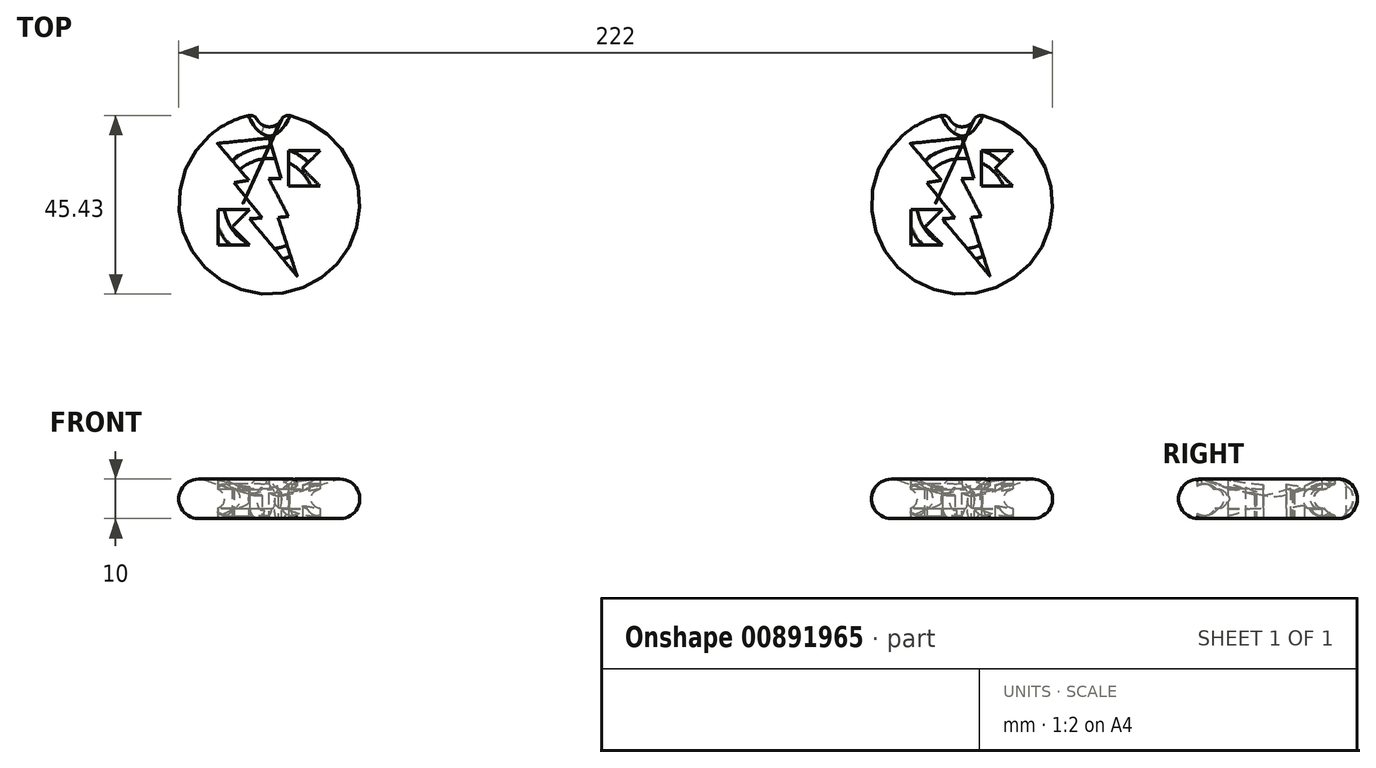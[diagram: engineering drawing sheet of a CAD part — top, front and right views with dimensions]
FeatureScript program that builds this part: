
annotation { "Feature Type Name" : "Feature", "Feature Type Description" : "" }
export const myFeature = defineFeature(function(context is Context, id is Id, definition is map)
    precondition{}
    {
        {
            var Q0;
            Q0=qCreatedBy(makeId("Right.planeOp"),FACE);
            var sketch = newSketch(context, id + "F0", { "sketchPlane" : qUnion([Q0])});
            skArc(sketch, "E0", {"start": v(-47.98, 20.03) * mm, "mid": v(-54.65, 16.24) * mm, "end": v(-49.73, 10.35) * mm});
            skArc(sketch, "E1", {"start": v(-47.98, 20.03) * mm, "mid": v(-39.95, 17.37) * mm, "end": v(-31.73, 15.35) * mm});
            skLineSegment(sketch, "E2", {"start": v(-31.73, 10.35) * mm, "end": v(-31.73, 15.35) * mm});
            skPoint(sketch, "E3.orphan", {"position": v(-49.73, 20.7) * mm});
            skLineSegment(sketch, "E4", {"start": v(-49.73, 10.35) * mm, "end": v(-31.73, 10.35) * mm});
            skSolve(sketch);
        }
        {
            var Q0;
            Q0 = qSketchRegion(id + "F0", true);
            var Q1;
            Q1=sQuery(id+"F0.wireOp",EDGE,"E2");
            revolve(context, id + "F1", {"surfaceOperationType" : NewSurfaceOperationType.NEW, "entities" : qUnion([Q0]), "axis" : qUnion([Q1]), "revolveType" : RevolveType.FULL});
        }
        {
            var Q0;
            Q0=qCreatedBy(makeId("Top.planeOp"),FACE);
            var sketch = newSketch(context, id + "F2", { "sketchPlane" : qUnion([Q0])});
            skLineSegment(sketch, "E5", {"start": v(-0.22, -15) * mm, "end": v(-0.08, -15.05) * mm});
            skLineSegment(sketch, "E6", {"start": v(-0.08, -15.05) * mm, "end": v(2.99, -25.32) * mm});
            skLineSegment(sketch, "E7", {"start": v(2.99, -25.32) * mm, "end": v(-0.17, -25.32) * mm});
            skLineSegment(sketch, "E8", {"start": v(-0.17, -25.32) * mm, "end": v(4.88, -34.98) * mm});
            skLineSegment(sketch, "E9", {"start": v(4.88, -34.98) * mm, "end": v(2.23, -35.23) * mm});
            skLineSegment(sketch, "E10", {"start": v(2.23, -35.23) * mm, "end": v(6.64, -48.88) * mm});
            skLineSegment(sketch, "E11", {"start": v(6.64, -48.88) * mm, "end": v(7.06, -50.02) * mm});
            skLineSegment(sketch, "E12", {"start": v(7.06, -50.02) * mm, "end": v(7.03, -50.1) * mm});
            skLineSegment(sketch, "E13", {"start": v(7.03, -50.1) * mm, "end": v(6.85, -50.03) * mm});
            skLineSegment(sketch, "E14", {"start": v(6.85, -50.03) * mm, "end": v(6.91, -49.95) * mm});
            skLineSegment(sketch, "E15", {"start": v(6.91, -49.95) * mm, "end": v(-5.04, -35.54) * mm});
            skLineSegment(sketch, "E16", {"start": v(-5.04, -35.54) * mm, "end": v(-1.78, -35.37) * mm});
            skLineSegment(sketch, "E17", {"start": v(-1.78, -35.37) * mm, "end": v(-8.99, -26.39) * mm});
            skLineSegment(sketch, "E18", {"start": v(-8.99, -26.39) * mm, "end": v(-5.22, -25.8) * mm});
            skLineSegment(sketch, "E19", {"start": v(-5.22, -25.8) * mm, "end": v(-13.02, -16.57) * mm});
            skLineSegment(sketch, "E20", {"start": v(-13.02, -16.57) * mm, "end": v(-13.18, -16.45) * mm});
            skLineSegment(sketch, "E21", {"start": v(-13.18, -16.45) * mm, "end": v(-13.17, -16.42) * mm});
            skLineSegment(sketch, "E22", {"start": v(-13.17, -16.42) * mm, "end": v(-0.81, -15.14) * mm});
            skLineSegment(sketch, "E23", {"start": v(-0.81, -15.14) * mm, "end": v(-0.14, -15.1) * mm});
            skLineSegment(sketch, "E24", {"start": v(-0.14, -15.1) * mm, "end": v(-0.22, -15) * mm});
            skLineSegment(sketch, "E25", {"start": v(4.88, -18.29) * mm, "end": v(12.88, -18.29) * mm});
            skLineSegment(sketch, "E26", {"start": v(12.88, -18.29) * mm, "end": v(8.38, -22.79) * mm});
            skLineSegment(sketch, "E27", {"start": v(8.38, -22.79) * mm, "end": v(12.88, -27.29) * mm});
            skLineSegment(sketch, "E28", {"start": v(12.88, -27.29) * mm, "end": v(4.88, -27.29) * mm});
            skLineSegment(sketch, "E29", {"start": v(4.88, -27.29) * mm, "end": v(4.88, -18.29) * mm});
            skLineSegment(sketch, "E30", {"start": v(-13.02, -33.24) * mm, "end": v(-5.02, -33.24) * mm});
            skLineSegment(sketch, "E31", {"start": v(-5.02, -33.24) * mm, "end": v(-9.52, -37.74) * mm});
            skLineSegment(sketch, "E32", {"start": v(-9.52, -37.74) * mm, "end": v(-5.02, -42.24) * mm});
            skLineSegment(sketch, "E33", {"start": v(-5.02, -42.24) * mm, "end": v(-13.02, -42.24) * mm});
            skLineSegment(sketch, "E34", {"start": v(-13.02, -42.24) * mm, "end": v(-13.02, -33.24) * mm});
            skSolve(sketch);
        }
        {
            var Q0;
            Q0 = qSketchRegion(id + "F2", true);
            extrude(context, id + "F3", {"entities" : qUnion([Q0]), "operationType" : NewBodyOperationType.REMOVE, "depth" : 25 * mm, "offsetDistance" : 25 * mm});
        }
        {
            var Q0;
            Q0=qCreatedBy(makeId("Right.planeOp"),FACE);
            var sketch = newSketch(context, id + "F4", { "sketchPlane" : qUnion([Q0])});
            skArc(sketch, "E35", {"start": v(-45.86, 12.85) * mm, "mid": v(-43.21, 15.52) * mm, "end": v(-46.2, 17.8) * mm});
            skLineSegment(sketch, "E36", {"start": v(-45.7, 15.35) * mm, "end": v(-48.7, 15.35) * mm, "construction": true});
            skArc(sketch, "E37", {"start": v(-46.2, 17.8) * mm, "mid": v(-53.33, 14.82) * mm, "end": v(-45.86, 12.85) * mm});
            skSolve(sketch);
        }
        {
            var Q0;
            Q0 = qSketchRegion(id + "F4", true);
            var Q1;
            Q1=sQuery(id+"F0.wireOp",EDGE,"E2");
            revolve(context, id + "F5", {"operationType" : NewBodyOperationType.ADD, "surfaceOperationType" : NewSurfaceOperationType.NEW, "entities" : qUnion([Q0]), "axis" : qUnion([Q1]), "revolveType" : RevolveType.FULL});
        }
        {
            var Q0;
            Q0=qCreatedBy(makeId("Top.planeOp"),FACE);
            var sketch = newSketch(context, id + "F6", { "sketchPlane" : qUnion([Q0])});
            skCircle(sketch, "E38", {"center": v(0, -8.71) * mm, "radius": 3.5 * mm});
            skSolve(sketch);
        }
        {
            var Q0;
            Q0 = qSketchRegion(id + "F6", true);
            extrude(context, id + "F7", {"entities" : qUnion([Q0]), "operationType" : NewBodyOperationType.REMOVE, "depth" : 25 * mm, "offsetDistance" : 25 * mm});
        }
        {
            var Q0;
            Q0=makeQuery(id+"F7.boolean.opBoolean","INTERSECT",EDGE,{"derivedFrom":[makeQuery(id+"F1.opRevolve","SWEPT_FACE",FACE,{"disambiguationData":[OSD([sQuery(id+"F0.wireOp",EDGE,"E0")])]}),makeQuery(id+"F7.opExtrude","SWEPT_FACE",FACE,{"disambiguationData":[OSD([sQuery(id+"F6.wireOp",EDGE,"E38")])]})]});
            fillet(context, id + "F8", {"entities" : qUnion([Q0]), "radius" : 2 * mm, "tangentPropagation" : true, "allowEdgeOverflow" : false});
        }
        {
            var Q0;
            Q0=makeQuery(id+"F1.opRevolve","SWEPT_BODY",BODY,{"disambiguationData":[OSD([sQuery(id+"F0.wireOp",EDGE,"E0"),sQuery(id+"F0.wireOp",EDGE,"E1"),sQuery(id+"F0.wireOp",EDGE,"pKwaynfI-0gC1-n2Fh-BdSd-cLsVGHjrdETn"),sQuery(id+"F0.wireOp",EDGE,"E2")])]});
            transform(context, id + "F9", {"entities" : qUnion([Q0]), "transformType" : TransformType.TRANSLATION_3D, "dx" : 176 * mm, "dy" : 0 * mm, "dz" : 0 * mm, "makeCopy" : true});
        }
    });
